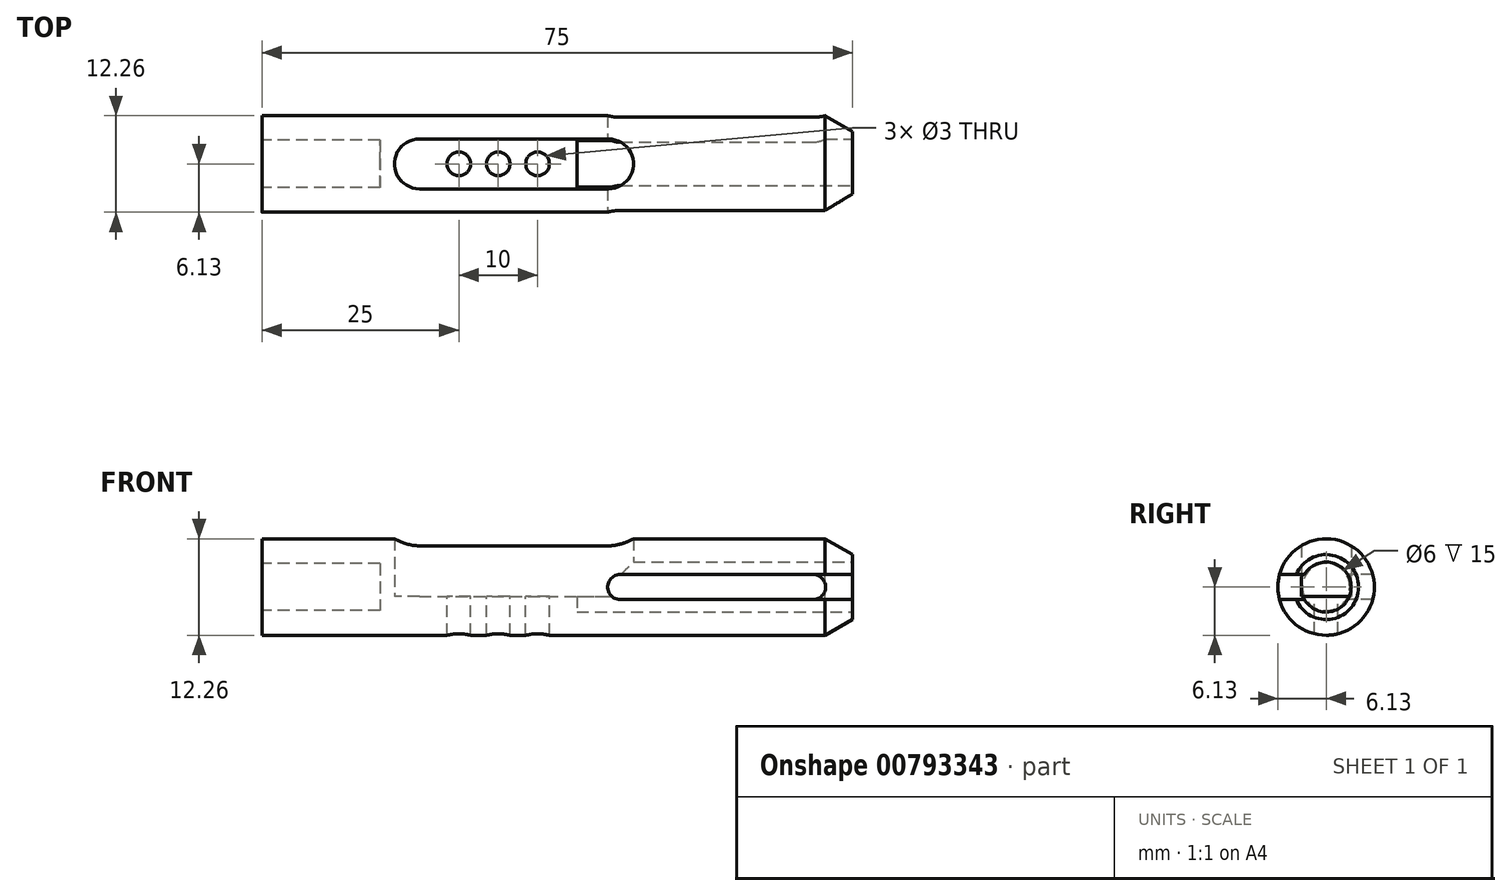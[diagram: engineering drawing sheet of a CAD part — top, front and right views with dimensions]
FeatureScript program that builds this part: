
annotation { "Feature Type Name" : "Feature", "Feature Type Description" : "" }
export const myFeature = defineFeature(function(context is Context, id is Id, definition is map)
    precondition{}
    {
        {
            var Q0;
            Q0=qCreatedBy(makeId("Right.planeOp"),FACE);
            var sketch = newSketch(context, id + "F0", { "sketchPlane" : qUnion([Q0])});
            skCircle(sketch, "E0", {"center": v(0, 0) * mm, "radius": 6.13 * mm});
            skSolve(sketch);
        }
        {
            var Q0;
            Q0 = qSketchRegion(id + "F0", true);
            extrude(context, id + "F1", {"entities" : qUnion([Q0]), "depth" : 75 * mm, "offsetDistance" : 25 * mm});
        }
        {
            var Q0;
            Q0=makeQuery(id+"F1.opExtrude","CAP_FACE",FACE,{"disambiguationData":[OSD([sQuery(id+"F0.wireOp",EDGE,"E0")])],"isStart":false});
            var sketch = newSketch(context, id + "F2", { "sketchPlane" : qUnion([Q0])});
            skCircle(sketch, "E1", {"center": v(0, 0) * mm, "radius": 3.18 * mm});
            skSolve(sketch);
        }
        {
            var Q0;
            Q0 = qSketchRegion(id + "F2", true);
            extrude(context, id + "F3", {"entities" : qUnion([Q0]), "operationType" : NewBodyOperationType.REMOVE, "oppositeDirection" : true, "depth" : 35 * mm, "offsetDistance" : 25 * mm});
        }
        {
            var Q0;
            Q0=makeQuery(id+"F1.opExtrude","CAP_FACE",FACE,{"disambiguationData":[OSD([sQuery(id+"F0.wireOp",EDGE,"E0")])],"isStart":true});
            var sketch = newSketch(context, id + "F4", { "sketchPlane" : qUnion([Q0])});
            skCircle(sketch, "E2", {"center": v(0, 0) * mm, "radius": 3 * mm});
            skSolve(sketch);
        }
        {
            var Q0;
            Q0 = qSketchRegion(id + "F4", true);
            extrude(context, id + "F5", {"entities" : qUnion([Q0]), "operationType" : NewBodyOperationType.REMOVE, "oppositeDirection" : true, "depth" : 15 * mm, "offsetDistance" : 25 * mm});
        }
        {
            var Q0;
            Q0=makeQuery(id+"F1.opExtrude","CAP_EDGE",EDGE,{"disambiguationData":[OSD([sQuery(id+"F0.wireOp",EDGE,"E0")])],"isStart":false});
            chamfer(context, id + "F6", {"entities" : qUnion([Q0]), "chamferType" : ChamferType.OFFSET_ANGLE, "width" : 2 * mm, "oppositeDirection" : false, "angle" : 60 * degree});
        }
        {
            var Q0;
            Q0=qCreatedBy(makeId("Top.planeOp"),FACE);
            var sketch = newSketch(context, id + "F7", { "sketchPlane" : qUnion([Q0])});
            skArc(sketch, "E3", {"start": v(20, 3.18) * mm, "mid": v(16.82, 0) * mm, "end": v(20, -3.17) * mm});
            skArc(sketch, "E4", {"start": v(44, -3.18) * mm, "mid": v(47.17, 0) * mm, "end": v(44, 3.17) * mm});
            skLineSegment(sketch, "E5", {"start": v(20, 3.18) * mm, "end": v(44, 3.18) * mm});
            skLineSegment(sketch, "E6", {"start": v(20, -3.18) * mm, "end": v(44, -3.18) * mm});
            skLineSegment(sketch, "E7", {"start": v(44, -3.17) * mm, "end": v(20, -3.18) * mm});
            skSolve(sketch);
        }
        {
            var Q0;
            Q0 = qSketchRegion(id + "F7", true);
            extrude(context, id + "F8", {"entities" : qUnion([Q0]), "operationType" : NewBodyOperationType.REMOVE, "endBound" : BoundingType.THROUGH_ALL, "depth" : 25 * mm, "offsetDistance" : 25 * mm, "hasSecondDirection" : true, "secondDirectionOppositeDirection" : true, "secondDirectionDepth" : 1.17 * mm});
        }
        {
            var Q0;
            Q0=qCreatedBy(makeId("Front.planeOp"),FACE);
            var sketch = newSketch(context, id + "F9", { "sketchPlane" : qUnion([Q0])});
            skArc(sketch, "E8", {"start": v(45.5, 1.59) * mm, "mid": v(43.91, 0) * mm, "end": v(45.5, -1.59) * mm});
            skArc(sketch, "E9", {"start": v(70, -1.59) * mm, "mid": v(71.59, 0) * mm, "end": v(70, 1.59) * mm});
            skLineSegment(sketch, "E10", {"start": v(45.5, 1.59) * mm, "end": v(70, 1.59) * mm});
            skLineSegment(sketch, "E11", {"start": v(45.5, -1.59) * mm, "end": v(70, -1.59) * mm});
            skSolve(sketch);
        }
        {
            var Q0;
            Q0 = qSketchRegion(id + "F9", true);
            extrude(context, id + "F10", {"entities" : qUnion([Q0]), "operationType" : NewBodyOperationType.REMOVE, "endBound" : BoundingType.THROUGH_ALL, "oppositeDirection" : true, "depth" : 25 * mm, "offsetDistance" : 25 * mm, "hasSecondDirection" : true, "secondDirectionBound" : SecondDirectionBoundingType.THROUGH_ALL, "secondDirectionOppositeDirection" : false, "secondDirectionDepth" : 25 * mm});
        }
        {
            var Q0;
            Q0=qCreatedBy(makeId("Front.planeOp"),FACE);
            var sketch = newSketch(context, id + "F11", { "sketchPlane" : qUnion([Q0])});
            skLineSegment(sketch, "E12.bottom", {"start": v(63, 1.59) * mm, "end": v(78, 1.59) * mm});
            skLineSegment(sketch, "E12.top", {"start": v(63, -1.59) * mm, "end": v(78, -1.59) * mm});
            skLineSegment(sketch, "E12.left", {"start": v(63, 1.59) * mm, "end": v(63, -1.59) * mm});
            skLineSegment(sketch, "E12.right", {"start": v(78, 1.59) * mm, "end": v(78, -1.59) * mm});
            skSolve(sketch);
        }
        {
            var Q0;
            Q0 = qSketchRegion(id + "F11", true);
            extrude(context, id + "F12", {"entities" : qUnion([Q0]), "operationType" : NewBodyOperationType.REMOVE, "depth" : 25 * mm, "offsetDistance" : 25 * mm});
        }
        {
            var Q0;
            Q0=makeQuery(id+"F8.boolean.opBoolean","COPY",FACE,{"derivedFrom":makeQuery(id+"F8.opExtrude","CAP_FACE",FACE,{"disambiguationData":[OSD([sQuery(id+"F7.wireOp",EDGE,"E3"),sQuery(id+"F7.wireOp",EDGE,"E4"),sQuery(id+"F7.wireOp",EDGE,"E5"),sQuery(id+"F7.wireOp",EDGE,"E7")])],"isStart":true})});
            var sketch = newSketch(context, id + "F13", { "sketchPlane" : qUnion([Q0])});
            skCircle(sketch, "E13", {"center": v(25, 0) * mm, "radius": 1.5 * mm});
            skCircle(sketch, "E14", {"center": v(30, 0) * mm, "radius": 1.5 * mm});
            skCircle(sketch, "E15", {"center": v(35, 0) * mm, "radius": 1.5 * mm});
            skSolve(sketch);
        }
        {
            var Q0;
            Q0 = qSketchRegion(id + "F13", true);
            extrude(context, id + "F14", {"entities" : qUnion([Q0]), "operationType" : NewBodyOperationType.REMOVE, "endBound" : BoundingType.THROUGH_ALL, "oppositeDirection" : true, "depth" : 25 * mm, "offsetDistance" : 25 * mm});
        }
    });
